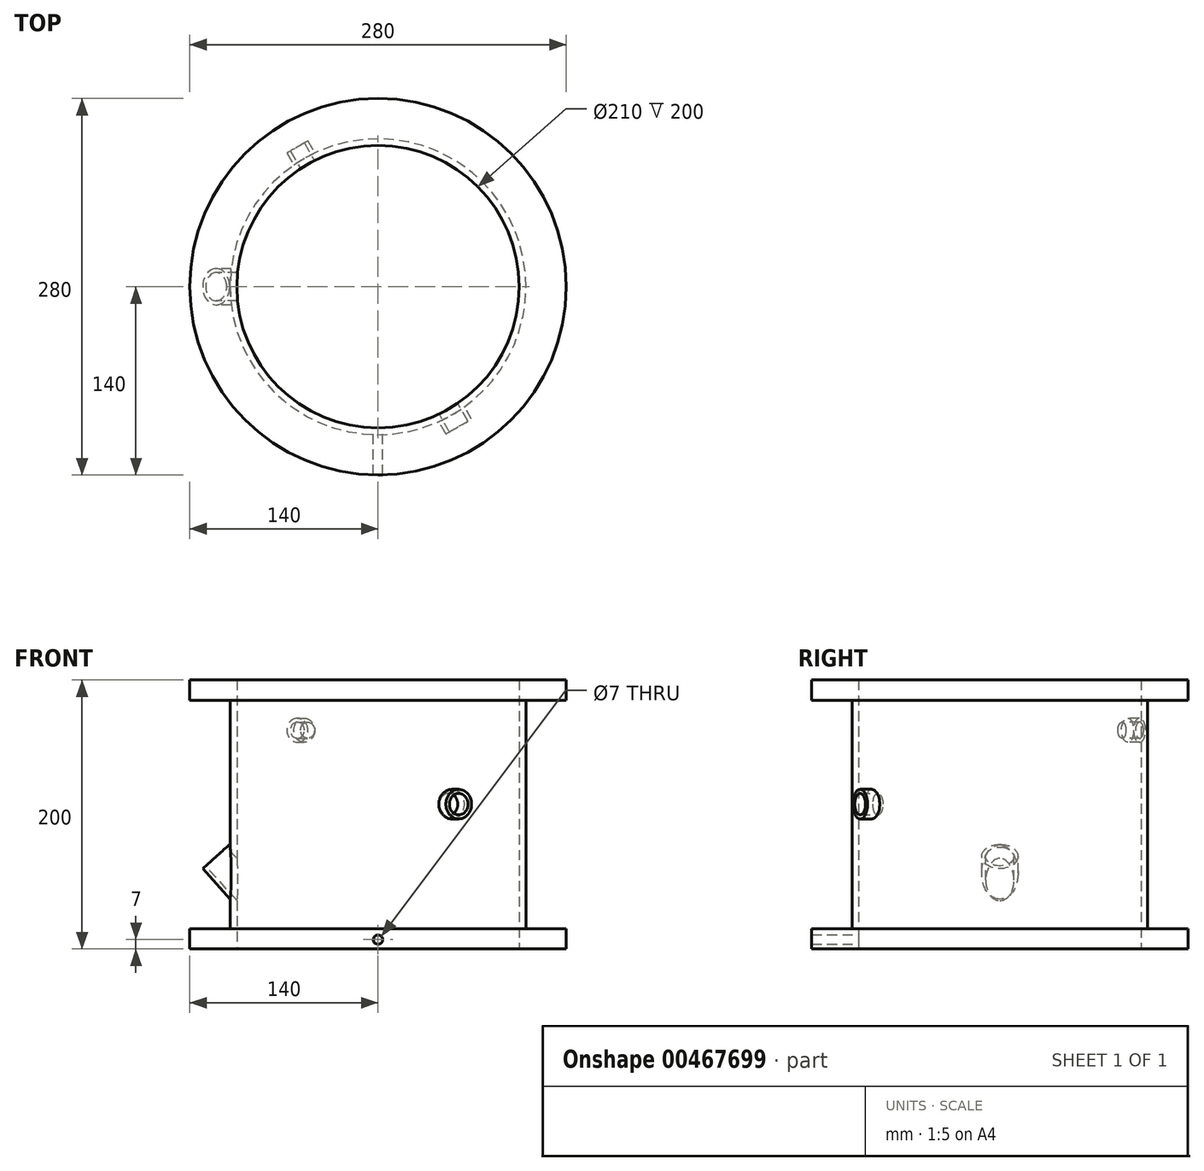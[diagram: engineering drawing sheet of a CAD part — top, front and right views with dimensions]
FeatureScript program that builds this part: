
annotation { "Feature Type Name" : "Feature", "Feature Type Description" : "" }
export const myFeature = defineFeature(function(context is Context, id is Id, definition is map)
    precondition{}
    {
        {
            var Q0;
            Q0=qCreatedBy(makeId("Front.planeOp"),FACE);
            var sketch = newSketch(context, id + "F0", { "sketchPlane" : qUnion([Q0])});
            skLineSegment(sketch, "E0", {"start": v(0, 0) * mm, "end": v(105, 0) * mm, "construction": true});
            skLineSegment(sketch, "E1", {"start": v(105, 0) * mm, "end": v(140, 0) * mm});
            skLineSegment(sketch, "E2", {"start": v(140, 0) * mm, "end": v(140, 15) * mm});
            skLineSegment(sketch, "E3", {"start": v(140, 15) * mm, "end": v(110, 15) * mm});
            skLineSegment(sketch, "E4", {"start": v(110, 15) * mm, "end": v(110, 185) * mm});
            skLineSegment(sketch, "E5", {"start": v(110, 185) * mm, "end": v(140, 185) * mm});
            skLineSegment(sketch, "E6", {"start": v(140, 185) * mm, "end": v(140, 200) * mm});
            skLineSegment(sketch, "E7", {"start": v(140, 200) * mm, "end": v(105, 200) * mm});
            skLineSegment(sketch, "E8", {"start": v(105, 200) * mm, "end": v(105, 0) * mm});
            skLineSegment(sketch, "E9", {"start": v(140, 185) * mm, "end": v(140, 15) * mm, "construction": true});
            skLineSegment(sketch, "E10", {"start": v(0, 0) * mm, "end": v(0, 197.7) * mm, "construction": true});
            skLineSegment(sketch, "E11.bottom", {"start": v(105, 200) * mm, "end": v(85, 200) * mm});
            skLineSegment(sketch, "E11.top", {"start": v(105, 0) * mm, "end": v(85, 0) * mm});
            skLineSegment(sketch, "E11.right", {"start": v(85, 200) * mm, "end": v(85, 0) * mm});
            skSolve(sketch);
        }
        {
            var Q0;
            Q0=makeQuery(id+"F0.imprint","IMPRINT",FACE,{"disambiguationData":[TD([[makeQuery(id+"F0.imprint","IMPRINT",EDGE,{"derivedFrom":sQuery(id+"F0.wireOp",EDGE,"E1")}),1.0]])]});
            var Q1;
            Q1=sQuery(id+"F0.wireOp",EDGE,"E10");
            revolve(context, id + "F1", {"entities" : qUnion([Q0]), "axis" : qUnion([Q1]), "revolveType" : RevolveType.FULL});
        }
        {
            var Q0;
            Q0=qCreatedBy(makeId("Front.planeOp"),FACE);
            var sketch = newSketch(context, id + "F2", { "sketchPlane" : qUnion([Q0])});
            skCircle(sketch, "E12", {"center": v(0, 7) * mm, "radius": 3.5 * mm});
            skSolve(sketch);
        }
        {
            var Q0;
            Q0=qSketchRegion(id+"F2",true);
            extrude(context, id + "F3", {"entities" : qUnion([Q0]), "operationType" : NewBodyOperationType.REMOVE, "depth" : 150 * mm, "offsetDistance" : 25 * mm});
        }
        {
            var Q0;
            Q0=qCreatedBy(makeId("Front.planeOp"),FACE);
            var sketch = newSketch(context, id + "F4", { "sketchPlane" : qUnion([Q0])});
            skLineSegment(sketch, "E13", {"start": v(0, 77.7) * mm, "end": v(0, 60.53) * mm});
            skLineSegment(sketch, "E14", {"start": v(0, 77.7) * mm, "end": v(-105, 77.7) * mm});
            skLineSegment(sketch, "E15", {"start": v(-105, 77.7) * mm, "end": v(-105, 51.7) * mm});
            skLineSegment(sketch, "E16", {"start": v(-105, 51.7) * mm, "end": v(-120.4, 68.8) * mm});
            skLineSegment(sketch, "E17", {"start": v(-105, 51.7) * mm, "end": v(-105, 49.7) * mm});
            skLineSegment(sketch, "E18", {"start": v(-120.4, 68.8) * mm, "end": v(-110.36, 77.84) * mm});
            skSolve(sketch);
        }
        {
            var Q0;
            Q0=sQuery(id+"F4.wireOp",EDGE,"E18");
            cPlane(context, id + "F5", {"entities" : qUnion([Q0]), "cplaneType" : CPlaneType.LINE_ANGLE, "offset" : 25 * mm, "angle" : 90 * degree, "width" : 150 * mm, "height" : 150 * mm});
        }
        {
            var Q0;
            Q0=qCreatedBy(id+"F5.planeOp",FACE);
            var sketch = newSketch(context, id + "F6", { "sketchPlane" : qUnion([Q0])});
            skCircle(sketch, "E19", {"center": v(-43.43, 0) * mm, "radius": 13.5 * mm});
            skCircle(sketch, "E20.0", {"center": v(-43.43, 0) * mm, "radius": 10.5 * mm});
            skSolve(sketch);
        }
        {
            var Q0;
            Q0=makeQuery(id+"F6.imprint","IMPRINT",FACE,{"disambiguationData":[TD([[makeQuery(id+"F6.imprint","IMPRINT",EDGE,{"derivedFrom":sQuery(id+"F6.wireOp",EDGE,"E19")}),1.0]])]});
            extrude(context, id + "F7", {"entities" : qUnion([Q0]), "operationType" : NewBodyOperationType.ADD, "oppositeDirection" : true, "depth" : 31 * mm});
        }
        {
            var Q0;
            Q0=makeQuery(id+"F0.imprint","IMPRINT",FACE,{"disambiguationData":[TD([[makeQuery(id+"F0.imprint","IMPRINT",EDGE,{"derivedFrom":sQuery(id+"F0.wireOp",EDGE,"E11.bottom")}),1.0]])]});
            var Q1;
            Q1=sQuery(id+"F0.wireOp",EDGE,"E10");
            revolve(context, id + "F8", {"operationType" : NewBodyOperationType.REMOVE, "entities" : qUnion([Q0]), "axis" : qUnion([Q1]), "revolveType" : RevolveType.FULL, "oppositeDirection" : true});
        }
        {
            var Q0;
            Q0=qCreatedBy(makeId("Top.planeOp"),FACE);
            var sketch = newSketch(context, id + "F9", { "sketchPlane" : qUnion([Q0])});
            skLineSegment(sketch, "E21", {"start": v(0, 0) * mm, "end": v(-24.71, 42.8) * mm});
            skLineSegment(sketch, "E22", {"start": v(0, 0) * mm, "end": v(0, 44.2) * mm});
            skSolve(sketch);
        }
        {
            var Q0;
            Q0=sQuery(id+"F9.wireOp",EDGE,"E21");
            cPlane(context, id + "F10", {"entities" : qUnion([Q0]), "cplaneType" : CPlaneType.LINE_ANGLE, "offset" : 25 * mm, "angle" : 90 * degree, "width" : 150 * mm, "height" : 150 * mm});
        }
        {
            var Q0;
            Q0=qCreatedBy(id+"F10.planeOp",FACE);
            var sketch = newSketch(context, id + "F11", { "sketchPlane" : qUnion([Q0])});
            skLineSegment(sketch, "E23", {"start": v(0, 162.7) * mm, "end": v(105, 162.7) * mm});
            skLineSegment(sketch, "E24", {"start": v(105, 162.7) * mm, "end": v(120, 162.7) * mm});
            skLineSegment(sketch, "E25", {"start": v(0, 107.7) * mm, "end": v(-105, 107.7) * mm});
            skLineSegment(sketch, "E26", {"start": v(-105, 107.7) * mm, "end": v(-120, 107.7) * mm});
            skLineSegment(sketch, "E27", {"start": v(-105, 107.7) * mm, "end": v(-105, 118.7) * mm});
            skLineSegment(sketch, "E28", {"start": v(-105, 118.7) * mm, "end": v(-120, 118.7) * mm});
            skLineSegment(sketch, "E29", {"start": v(-120, 118.7) * mm, "end": v(-120, 115.7) * mm});
            skLineSegment(sketch, "E30", {"start": v(-120, 115.7) * mm, "end": v(-105, 115.7) * mm});
            skLineSegment(sketch, "E31", {"start": v(105, 162.7) * mm, "end": v(105, 171.7) * mm});
            skLineSegment(sketch, "E32", {"start": v(105, 171.7) * mm, "end": v(120, 171.7) * mm});
            skLineSegment(sketch, "E33", {"start": v(120, 171.7) * mm, "end": v(120, 168.7) * mm});
            skLineSegment(sketch, "E34", {"start": v(120, 168.7) * mm, "end": v(105, 168.7) * mm});
            skLineSegment(sketch, "E35.bottom", {"start": v(-98.9, 115.7) * mm, "end": v(-124.7, 115.7) * mm});
            skLineSegment(sketch, "E35.top", {"start": v(-98.9, 107.7) * mm, "end": v(-124.7, 107.7) * mm});
            skLineSegment(sketch, "E35.left", {"start": v(-98.9, 115.7) * mm, "end": v(-98.9, 107.7) * mm});
            skLineSegment(sketch, "E35.right", {"start": v(-124.7, 115.7) * mm, "end": v(-124.7, 107.7) * mm});
            skSolve(sketch);
        }
        {
            var Q0;
            {var subQ0=sQuery(id+"F11.wireOp",EDGE,"E32");Q0=makeQuery(id+"F11.imprint","IMPRINT",FACE,{"disambiguationData":[TD([[makeQuery(id+"F11.imprint","IMPRINT",EDGE,{"derivedFrom":subQ0}),-1.0]])]});}
            var Q1;
            Q1=sQuery(id+"F11.wireOp",EDGE,"E24");
            revolve(context, id + "F12", {"operationType" : NewBodyOperationType.ADD, "entities" : qUnion([Q0]), "axis" : qUnion([Q1]), "revolveType" : RevolveType.FULL});
        }
        {
            var Q0;
            {var subQ0=sQuery(id+"F11.wireOp",EDGE,"E28");Q0=makeQuery(id+"F11.imprint","IMPRINT",FACE,{"disambiguationData":[TD([[makeQuery(id+"F11.imprint","IMPRINT",EDGE,{"derivedFrom":subQ0}),1.0]])]});}
            var Q1;
            Q1=sQuery(id+"F11.wireOp",EDGE,"E26");
            revolve(context, id + "F13", {"operationType" : NewBodyOperationType.ADD, "entities" : qUnion([Q0]), "axis" : qUnion([Q1]), "revolveType" : RevolveType.FULL});
        }
        {
            var Q0;
            Q0=makeQuery(id+"F6.imprint","IMPRINT",FACE,{"disambiguationData":[TD([[makeQuery(id+"F6.imprint","IMPRINT",EDGE,{"derivedFrom":sQuery(id+"F6.wireOp",EDGE,"E20.0")}),1.0]])]});
            extrude(context, id + "F14", {"entities" : qUnion([Q0]), "operationType" : NewBodyOperationType.REMOVE, "oppositeDirection" : true, "depth" : 4000 * mm, "offsetDistance" : 25 * mm});
        }
        {
            var Q0;
            Q0=makeQuery(id+"F13.opRevolve","SWEPT_FACE",FACE,{"disambiguationData":[OSD([sQuery(id+"F11.wireOp",EDGE,"E29")])]});
            var sketch = newSketch(context, id + "F15", { "sketchPlane" : qUnion([Q0])});
            skCircle(sketch, "E36", {"center": v(0, 107.7) * mm, "radius": 8 * mm});
            skPoint(sketch, "E36.first.point", {"position": v(-7.9, 108.91) * mm});
            skPoint(sketch, "E36.second.point", {"position": v(3.04, 115.11) * mm});
            skPoint(sketch, "E36.third.point", {"position": v(4.75, 101.28) * mm});
            skSolve(sketch);
        }
        {
            var Q0;
            Q0=makeQuery(id+"F15.imprint","IMPRINT",FACE,{"disambiguationData":[TD([[makeQuery(id+"F15.imprint","IMPRINT",EDGE,{"derivedFrom":sQuery(id+"F15.wireOp",EDGE,"E36")}),-1.0]])]});
            extrude(context, id + "F16", {"entities" : qUnion([Q0]), "operationType" : NewBodyOperationType.REMOVE, "oppositeDirection" : true, "depth" : 25 * mm, "offsetDistance" : 25 * mm});
        }
        {
            var Q0;
            Q0=makeQuery(id+"F12.opRevolve","SWEPT_FACE",FACE,{"disambiguationData":[OSD([sQuery(id+"F11.wireOp",EDGE,"E33")])]});
            var sketch = newSketch(context, id + "F17", { "sketchPlane" : qUnion([Q0])});
            skCircle(sketch, "E37", {"center": v(0, 162.7) * mm, "radius": 6 * mm});
            skPoint(sketch, "E37.first.point", {"position": v(-5.95, 163.5) * mm});
            skPoint(sketch, "E37.second.point", {"position": v(2.1, 157.09) * mm});
            skPoint(sketch, "E37.third.point", {"position": v(3.59, 167.52) * mm});
            skSolve(sketch);
        }
        {
            var Q0;
            Q0=qSketchRegion(id+"F17",true);
            extrude(context, id + "F18", {"entities" : qUnion([Q0]), "operationType" : NewBodyOperationType.REMOVE, "oppositeDirection" : true, "depth" : 25 * mm, "offsetDistance" : 25 * mm});
        }
    });
